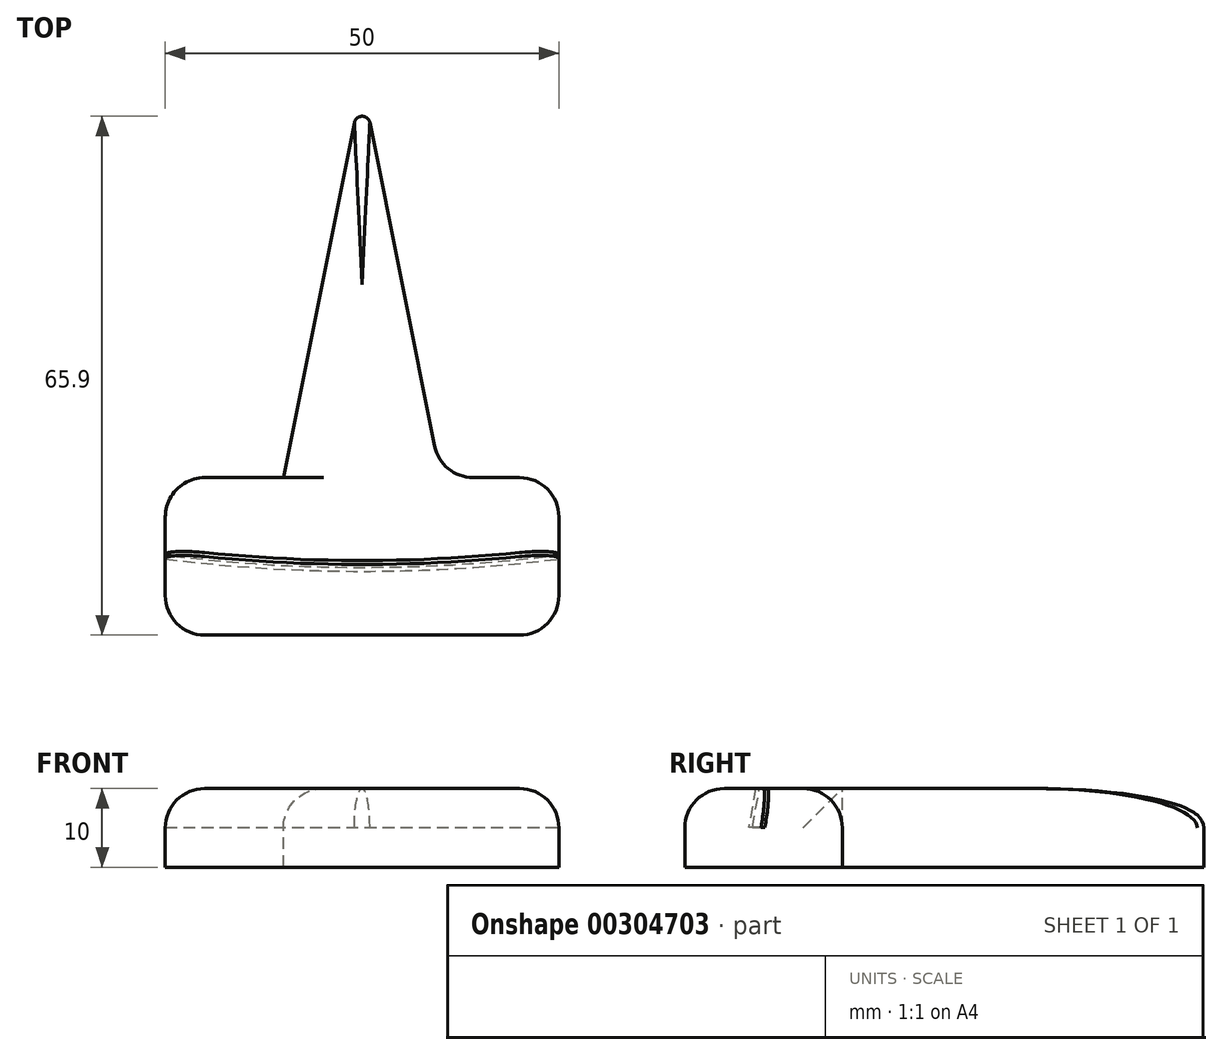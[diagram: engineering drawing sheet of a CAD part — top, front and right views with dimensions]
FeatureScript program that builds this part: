
annotation { "Feature Type Name" : "Feature", "Feature Type Description" : "" }
export const myFeature = defineFeature(function(context is Context, id is Id, definition is map)
    precondition{}
    {
        {
            var Q0;
            Q0=qCreatedBy(makeId("Top.planeOp"),FACE);
            var sketch = newSketch(context, id + "F0", { "sketchPlane" : qUnion([Q0])});
            skLineSegment(sketch, "E0.bottom", {"start": v(0, 0) * mm, "end": v(50, 0) * mm});
            skLineSegment(sketch, "E0.top", {"start": v(0, 20) * mm, "end": v(50, 20) * mm});
            skLineSegment(sketch, "E0.left", {"start": v(0, 0) * mm, "end": v(0, 20) * mm});
            skLineSegment(sketch, "E0.right", {"start": v(50, 0) * mm, "end": v(50, 20) * mm});
            skSolve(sketch);
        }
        {
            var Q0;
            Q0=makeQuery(id+"F0.imprint","IMPRINT",FACE,{"disambiguationData":[TD([[makeQuery(id+"F0.imprint","IMPRINT",EDGE,{"derivedFrom":sQuery(id+"F0.wireOp",EDGE,"E0.bottom")}),1.0]])]});
            extrude(context, id + "F1", {"entities" : qUnion([Q0]), "depth" : 10 * mm});
        }
        {
            var Q0;
            Q0=makeQuery(id+"F1.opExtrude","CAP_FACE",FACE,{"disambiguationData":[OSD([sQuery(id+"F0.wireOp",EDGE,"E0.bottom"),sQuery(id+"F0.wireOp",EDGE,"E0.top"),sQuery(id+"F0.wireOp",EDGE,"E0.left"),sQuery(id+"F0.wireOp",EDGE,"E0.right")])],"isStart":false});
            var sketch = newSketch(context, id + "F2", { "sketchPlane" : qUnion([Q0])});
            skCircle(sketch, "E1", {"center": v(25, 209.22) * mm, "radius": 200 * mm, "construction": true});
            skLineSegment(sketch, "E2", {"start": v(50, 10.78) * mm, "end": v(0, 10.78) * mm, "construction": true});
            skLineSegment(sketch, "E3", {"start": v(25, 10.78) * mm, "end": v(25, 9.22) * mm, "construction": true});
            skPoint(sketch, "E4", {"position": v(25, 10) * mm});
            skCircle(sketch, "E5.0", {"center": v(25, 209.22) * mm, "radius": 200.25 * mm});
            skCircle(sketch, "E6.0", {"center": v(25, 209.22) * mm, "radius": 199.75 * mm});
            skLineSegment(sketch, "E7", {"start": v(0, 11.04) * mm, "end": v(0, 10.53) * mm});
            skSolve(sketch);
        }
        {
            var Q0;
            Q0=makeQuery(id+"F1.opExtrude","SWEPT_FACE",FACE,{"disambiguationData":[OSD([sQuery(id+"F0.wireOp",EDGE,"E0.left")])]});
            var sketch = newSketch(context, id + "F3", { "sketchPlane" : qUnion([Q0])});
            skLineSegment(sketch, "E8", {"start": v(-10.53, 10) * mm, "end": v(-9.66, 5.08) * mm});
            skSolve(sketch);
        }
        {
            var Q0;
            {var subQ0=sQuery(id+"F2.wireOp",EDGE,"E7");Q0=makeQuery(id+"F2.imprint","IMPRINT",FACE,{"disambiguationData":[TD([[makeQuery(id+"F2.imprint","IMPRINT",EDGE,{"derivedFrom":subQ0}),-1.0]])]});}
            var Q1;
            Q1=sQuery(id+"F3.wireOp",EDGE,"E8");
            sweep(context, id + "F4", {"operationType" : NewBodyOperationType.REMOVE, "profiles" : qUnion([Q0]), "path" : qUnion([Q1])});
        }
        {
            var Q0;
            {var subQ0=sQuery(id+"F0.wireOp",EDGE,"E0.top");var subQ1=sQuery(id+"F0.wireOp",EDGE,"E0.left");var subQ2=sQuery(id+"F0.wireOp",EDGE,"E0.right");Q0=makeQuery(id+"F4.boolean.opBoolean","SPLIT",FACE,{"disambiguationData":[TD([makeQuery(id+"F1.opExtrude","SWEPT_FACE",FACE,{"disambiguationData":[OSD([subQ0])]})])],"derivedFrom":makeQuery(id+"F1.opExtrude","CAP_FACE",FACE,{"disambiguationData":[OSD([sQuery(id+"F0.wireOp",EDGE,"E0.bottom"),subQ0,subQ1,subQ2])],"isStart":false})});}
            var sketch = newSketch(context, id + "F5", { "sketchPlane" : qUnion([Q0])});
            skLineSegment(sketch, "E9", {"start": v(25, 70) * mm, "end": v(15, 20) * mm});
            skPoint(sketch, "E9.startSnap0", {"position": v(25, 20) * mm});
            skLineSegment(sketch, "E10", {"start": v(15, 20) * mm, "end": v(35, 20) * mm});
            skLineSegment(sketch, "E11", {"start": v(35, 20) * mm, "end": v(25, 70) * mm});
            skSolve(sketch);
        }
        {
            var Q0;
            Q0=makeQuery(id+"F5.imprint","IMPRINT",FACE,{"disambiguationData":[TD([[makeQuery(id+"F5.imprint","IMPRINT",EDGE,{"derivedFrom":sQuery(id+"F5.wireOp",EDGE,"E9")}),1.0]])]});
            var Q1;
            Q1=makeQuery(id+"F1.opExtrude","CAP_FACE",FACE,{"disambiguationData":[OSD([sQuery(id+"F0.wireOp",EDGE,"E0.bottom"),sQuery(id+"F0.wireOp",EDGE,"E0.top"),sQuery(id+"F0.wireOp",EDGE,"E0.left"),sQuery(id+"F0.wireOp",EDGE,"E0.right")])],"isStart":true});
            extrude(context, id + "F6", {"entities" : qUnion([Q0]), "operationType" : NewBodyOperationType.ADD, "endBound" : BoundingType.UP_TO_SURFACE, "oppositeDirection" : true, "endBoundEntityFace" : qUnion([Q1]), "depth" : 20.9 * mm});
        }
        {
            var Q0;
            Q0=makeQuery(id+"F1.opExtrude","SWEPT_EDGE",EDGE,{"disambiguationData":[OSD([sQuery(id+"F0.wireOp",EDGE,"E0.bottom"),sQuery(id+"F0.wireOp",EDGE,"E0.right")])]});
            var Q1;
            Q1=makeQuery(id+"F1.opExtrude","SWEPT_EDGE",EDGE,{"disambiguationData":[OSD([sQuery(id+"F0.wireOp",EDGE,"E0.top"),sQuery(id+"F0.wireOp",EDGE,"E0.right")])]});
            var Q2;
            Q2=makeQuery(id+"F6.opExtrude","SWEPT_EDGE",EDGE,{"disambiguationData":[OSD([sQuery(id+"F0.wireOp",EDGE,"E0.top"),sQuery(id+"F5.wireOp",EDGE,"E10"),sQuery(id+"F5.wireOp",EDGE,"E11")])]});
            var Q3;
            Q3=makeQuery(id+"F1.opExtrude","SWEPT_EDGE",EDGE,{"disambiguationData":[OSD([sQuery(id+"F0.wireOp",EDGE,"E0.top"),sQuery(id+"F0.wireOp",EDGE,"E0.left")])]});
            var Q4;
            Q4=makeQuery(id+"F6.opExtrude","SWEPT_EDGE",EDGE,{"disambiguationData":[OSD([sQuery(id+"F0.wireOp",EDGE,"E0.top"),sQuery(id+"F5.wireOp",EDGE,"E9"),sQuery(id+"F5.wireOp",EDGE,"E10")])]});
            var Q5;
            Q5=makeQuery(id+"F1.opExtrude","SWEPT_EDGE",EDGE,{"disambiguationData":[OSD([sQuery(id+"F0.wireOp",EDGE,"E0.bottom"),sQuery(id+"F0.wireOp",EDGE,"E0.left")])]});
            fillet(context, id + "F7", {"entities" : qUnion([Q0, Q1, Q2, Q3, Q4, Q5]), "radius" : 5 * mm, "tangentPropagation" : true, "allowEdgeOverflow" : false});
        }
        {
            var Q0;
            Q0=makeQuery(id+"F6.opExtrude","SWEPT_EDGE",EDGE,{"disambiguationData":[OSD([sQuery(id+"F5.wireOp",EDGE,"E9"),sQuery(id+"F5.wireOp",EDGE,"E11")])]});
            fillet(context, id + "F8", {"entities" : qUnion([Q0]), "radius" : 1 * mm, "tangentPropagation" : true, "allowEdgeOverflow" : false});
        }
        {
            var Q0;
            Q0=makeQuery(id+"F1.opExtrude","CAP_EDGE",EDGE,{"disambiguationData":[OSD([sQuery(id+"F0.wireOp",EDGE,"E0.bottom")])],"isStart":false});
            var Q1;
            Q1=makeQuery(id+"F6.opExtrude","CAP_EDGE",EDGE,{"disambiguationData":[OSD([sQuery(id+"F5.wireOp",EDGE,"E11")])],"isStart":true});
            fillet(context, id + "F9", {"entities" : qUnion([Q0, Q1]), "radius" : 5 * mm, "tangentPropagation" : true, "allowEdgeOverflow" : false});
        }
    });
